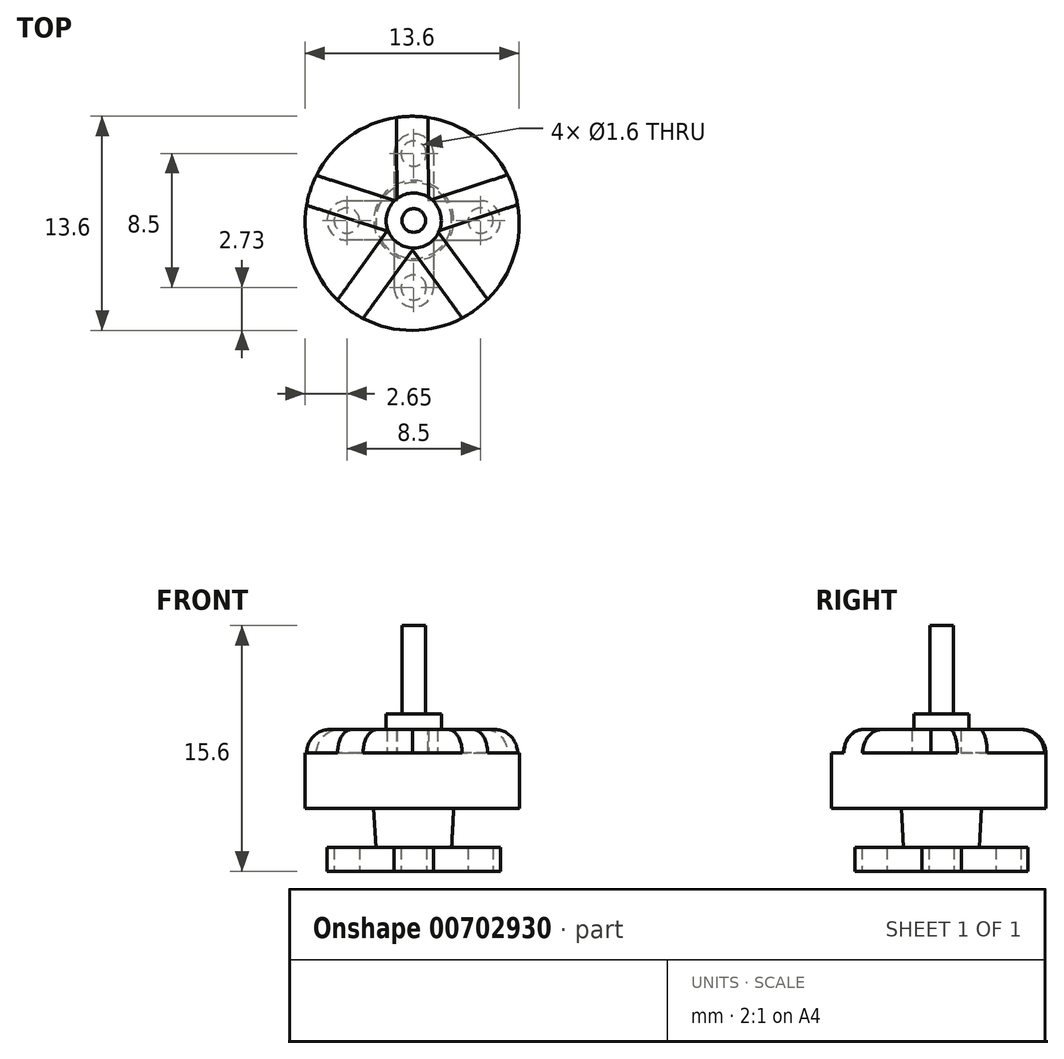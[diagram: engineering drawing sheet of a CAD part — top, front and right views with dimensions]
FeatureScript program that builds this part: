
annotation { "Feature Type Name" : "Feature", "Feature Type Description" : "" }
export const myFeature = defineFeature(function(context is Context, id is Id, definition is map)
    precondition{}
    {
        {
            var Q0;
            Q0=qCreatedBy(makeId("Top.planeOp"),FACE);
            var sketch = newSketch(context, id + "F0", { "sketchPlane" : qUnion([Q0])});
            skLineSegment(sketch, "E0.bottom", {"start": v(0, 0) * mm, "end": v(0, 0) * mm});
            skCircle(sketch, "E1", {"center": v(0, 4.25) * mm, "radius": 0.8 * mm});
            skLineSegment(sketch, "E2", {"start": v(0, 4.25) * mm, "end": v(0, 4.25) * mm});
            skCircle(sketch, "E3", {"center": v(0, -4.25) * mm, "radius": 0.8 * mm});
            skLineSegment(sketch, "E4", {"start": v(0, -4.25) * mm, "end": v(0, -4.25) * mm});
            skLineSegment(sketch, "E5.bottom", {"start": v(0, 1.25) * mm, "end": v(0, -1.25) * mm});
            skLineSegment(sketch, "E5.left", {"start": v(0, 1.25) * mm, "end": v(4.25, 1.25) * mm});
            skLineSegment(sketch, "E5.right", {"start": v(0, -1.25) * mm, "end": v(4.25, -1.25) * mm});
            skCircle(sketch, "E6", {"center": v(4.25, 0) * mm, "radius": 0.8 * mm});
            skArc(sketch, "E7", {"start": v(4.25, 1.25) * mm, "mid": v(5.5, 0) * mm, "end": v(4.25, -1.25) * mm});
            skPoint(sketch, "E8", {"position": v(0, 0) * mm});
            skLineSegment(sketch, "E9.left", {"start": v(0, -1.25) * mm, "end": v(-4.25, -1.25) * mm});
            skLineSegment(sketch, "E9.right", {"start": v(0, 1.25) * mm, "end": v(-4.25, 1.25) * mm});
            skCircle(sketch, "E10", {"center": v(-4.25, 0) * mm, "radius": 0.8 * mm});
            skArc(sketch, "E11", {"start": v(-4.25, -1.25) * mm, "mid": v(-5.5, 0) * mm, "end": v(-4.25, 1.25) * mm});
            skLineSegment(sketch, "E12", {"start": v(-1.25, 4.25) * mm, "end": v(-1.25, 1.25) * mm});
            skLineSegment(sketch, "E13", {"start": v(1.25, 4.25) * mm, "end": v(1.25, 1.25) * mm});
            skArc(sketch, "E14", {"start": v(-1.25, 4.25) * mm, "mid": v(0, 5.5) * mm, "end": v(1.25, 4.25) * mm});
            skLineSegment(sketch, "E15", {"start": v(-1.25, -1.25) * mm, "end": v(-1.25, -4.25) * mm});
            skLineSegment(sketch, "E16", {"start": v(1.25, -1.25) * mm, "end": v(1.25, -4.25) * mm});
            skArc(sketch, "E17", {"start": v(1.25, -4.25) * mm, "mid": v(0, -5.5) * mm, "end": v(-1.25, -4.25) * mm});
            skSolve(sketch);
        }
        {
            var Q0;
            {var subQ1=sQuery(id+"F0.wireOp",EDGE,"E5.bottom");Q0=makeQuery(id+"F0.imprint","IMPRINT",FACE,{"disambiguationData":[TD([[makeQuery(id+"F0.imprint","IMPRINT",EDGE,{"derivedFrom":subQ1}),-1.0]])]});}
            var Q1;
            Q1=makeQuery(id+"F0.imprint","IMPRINT",FACE,{"disambiguationData":[TD([[makeQuery(id+"F0.imprint","IMPRINT",EDGE,{"derivedFrom":sQuery(id+"F0.wireOp",EDGE,"E3")}),-1.0]])]});
            var Q2;
            {var subQ1=sQuery(id+"F0.wireOp",EDGE,"E5.bottom");Q2=makeQuery(id+"F0.imprint","IMPRINT",FACE,{"disambiguationData":[TD([[makeQuery(id+"F0.imprint","IMPRINT",EDGE,{"derivedFrom":subQ1}),1.0]])]});}
            var Q3;
            Q3=makeQuery(id+"F0.imprint","IMPRINT",FACE,{"disambiguationData":[TD([[makeQuery(id+"F0.imprint","IMPRINT",EDGE,{"derivedFrom":sQuery(id+"F0.wireOp",EDGE,"E1")}),-1.0]])]});
            extrude(context, id + "F1", {"entities" : qUnion([Q0, Q1, Q2, Q3]), "depth" : 1.5 * mm, "offsetDistance" : 25 * mm});
        }
        {
            var Q0;
            Q0=qCreatedBy(makeId("Top.planeOp"),FACE);
            var sketch = newSketch(context, id + "F2", { "sketchPlane" : qUnion([Q0])});
            skCircle(sketch, "E18", {"center": v(0, 0) * mm, "radius": 2.33 * mm});
            skSolve(sketch);
        }
        {
            var Q0;
            Q0=qSketchRegion(id+"F2",true);
            extrude(context, id + "F3", {"entities" : qUnion([Q0]), "operationType" : NewBodyOperationType.ADD, "depth" : 4 * mm, "offsetDistance" : 25 * mm, "hasDraft" : true, "draftAngle" : 3 * degree, "hasSecondDirection" : true, "secondDirectionOppositeDirection" : true, "secondDirectionDepth" : -1.5 * mm});
        }
        {
            var Q0;
            Q0=qCreatedBy(makeId("Top.planeOp"),FACE);
            var sketch = newSketch(context, id + "F4", { "sketchPlane" : qUnion([Q0])});
            skCircle(sketch, "E19", {"center": v(-0.1, -0.18) * mm, "radius": 6.8 * mm});
            skLineSegment(sketch, "E20", {"start": v(-4.84, -5.05) * mm, "end": v(-1.07, 0.18) * mm});
            skLineSegment(sketch, "E21", {"start": v(-3.22, -6.22) * mm, "end": v(0.56, -0.98) * mm});
            skLineSegment(sketch, "E22", {"start": v(0.56, -0.98) * mm, "end": v(6.6, 1) * mm});
            skLineSegment(sketch, "E23", {"start": v(5.96, 2.9) * mm, "end": v(-0.09, 0.91) * mm});
            skLineSegment(sketch, "E24", {"start": v(-0.09, 0.91) * mm, "end": v(-6.18, 2.87) * mm});
            skLineSegment(sketch, "E25", {"start": v(-6.8, 0.96) * mm, "end": v(-0.74, -0.98) * mm});
            skLineSegment(sketch, "E26", {"start": v(-0.74, -0.98) * mm, "end": v(3.08, -6.2) * mm});
            skLineSegment(sketch, "E27", {"start": v(4.7, -5) * mm, "end": v(0.93, 0.12) * mm});
            skLineSegment(sketch, "E28", {"start": v(0.93, 0.12) * mm, "end": v(0.9, 6.54) * mm});
            skLineSegment(sketch, "E29", {"start": v(-1.1, 6.55) * mm, "end": v(-1.07, 0.18) * mm});
            skPoint(sketch, "E30", {"position": v(-1.07, 1.23) * mm});
            skPoint(sketch, "E31", {"position": v(0.93, 1.25) * mm});
            skPoint(sketch, "E32", {"position": v(1.51, -0.67) * mm});
            skPoint(sketch, "E33", {"position": v(-0.08, -1.87) * mm});
            skPoint(sketch, "E34", {"position": v(-1.69, -0.68) * mm});
            skSolve(sketch);
        }
        {
            var Q0;
            Q0=makeQuery(id+"F4.imprint","IMPRINT",FACE,{"disambiguationData":[TD([[makeQuery(id+"F4.imprint","IMPRINT",EDGE,{"derivedFrom":sQuery(id+"F4.wireOp",EDGE,"CS8Gledc-ocEL-GRrZ-OUe9-gGzYdw9osQ4W")}),1.0]])]});
            var Q1;
            {var subQ0=sQuery(id+"F4.wireOp",EDGE,"E24");var subQ1=sQuery(id+"F4.wireOp",EDGE,"E19");var subQ2=makeQuery(id+"F4.imprint","INTERSECT",VERTEX,{"derivedFrom":[subQ1,subQ0]});Q1=makeQuery(id+"F4.imprint","IMPRINT",FACE,{"disambiguationData":[TD([[makeQuery(id+"F4.imprint","IMPRINT",EDGE,{"disambiguationData":[TD([[subQ2,1.0]])],"derivedFrom":subQ1}),1.0]])]});}
            var Q2;
            {var subQ0=sQuery(id+"F4.wireOp",EDGE,"E23");var subQ1=sQuery(id+"F4.wireOp",EDGE,"E19");var subQ2=makeQuery(id+"F4.imprint","INTERSECT",VERTEX,{"derivedFrom":[subQ1,subQ0]});Q2=makeQuery(id+"F4.imprint","IMPRINT",FACE,{"disambiguationData":[TD([[makeQuery(id+"F4.imprint","IMPRINT",EDGE,{"disambiguationData":[TD([[subQ2,-1.0]])],"derivedFrom":subQ1}),1.0]])]});}
            var Q3;
            {var subQ0=sQuery(id+"F4.wireOp",EDGE,"E22");var subQ1=sQuery(id+"F4.wireOp",EDGE,"E19");var subQ2=makeQuery(id+"F4.imprint","INTERSECT",VERTEX,{"derivedFrom":[subQ1,subQ0]});Q3=makeQuery(id+"F4.imprint","IMPRINT",FACE,{"disambiguationData":[TD([[makeQuery(id+"F4.imprint","IMPRINT",EDGE,{"disambiguationData":[TD([[subQ2,1.0]])],"derivedFrom":subQ1}),1.0]])]});}
            var Q4;
            {var subQ0=sQuery(id+"F4.wireOp",EDGE,"E21");var subQ1=sQuery(id+"F4.wireOp",EDGE,"E19");var subQ2=makeQuery(id+"F4.imprint","INTERSECT",VERTEX,{"derivedFrom":[subQ1,subQ0]});Q4=makeQuery(id+"F4.imprint","IMPRINT",FACE,{"disambiguationData":[TD([[makeQuery(id+"F4.imprint","IMPRINT",EDGE,{"disambiguationData":[TD([[subQ2,-1.0]])],"derivedFrom":subQ1}),1.0]])]});}
            var Q5;
            {var subQ0=sQuery(id+"F4.wireOp",EDGE,"E20");var subQ1=sQuery(id+"F4.wireOp",EDGE,"E19");var subQ2=makeQuery(id+"F4.imprint","INTERSECT",VERTEX,{"derivedFrom":[subQ1,subQ0]});Q5=makeQuery(id+"F4.imprint","IMPRINT",FACE,{"disambiguationData":[TD([[makeQuery(id+"F4.imprint","IMPRINT",EDGE,{"disambiguationData":[TD([[subQ2,1.0]])],"derivedFrom":subQ1}),1.0]])]});}
            extrude(context, id + "F5", {"entities" : qUnion([Q0, Q1, Q2, Q3, Q4, Q5]), "operationType" : NewBodyOperationType.ADD, "depth" : 7.5 * mm, "offsetDistance" : 25 * mm, "hasSecondDirection" : true, "secondDirectionOppositeDirection" : false, "secondDirectionDepth" : 4 * mm});
        }
        {
            var Q0;
            {var subQ5=sQuery(id+"F4.wireOp",EDGE,"k3woJ1cC-TIMz-5FnJ-hXcG-qWgU7OcKqM6W");var subQ6=sQuery(id+"F4.wireOp",EDGE,"CS8Gledc-ocEL-GRrZ-OUe9-gGzYdw9osQ4W");var subQ7=makeQuery(id+"F4.imprint","INTERSECT",VERTEX,{"derivedFrom":[subQ6,subQ5]});Q0=makeQuery(id+"F4.imprint","IMPRINT",FACE,{"disambiguationData":[TD([[makeQuery(id+"F4.imprint","IMPRINT",EDGE,{"disambiguationData":[TD([[subQ7,-1.0]])],"derivedFrom":subQ6}),1.0]])]});}
            var Q1;
            {var subQ1=sQuery(id+"F4.wireOp",EDGE,"CS8Gledc-ocEL-GRrZ-OUe9-gGzYdw9osQ4W");var subQ5=sQuery(id+"F4.wireOp",EDGE,"syxK5ZXx-2APs-c3Oq-3aUw-kv2rdBUAnRqm");var subQ6=makeQuery(id+"F4.imprint","INTERSECT",VERTEX,{"derivedFrom":[subQ1,subQ5]});Q1=makeQuery(id+"F4.imprint","IMPRINT",FACE,{"disambiguationData":[TD([[makeQuery(id+"F4.imprint","IMPRINT",EDGE,{"disambiguationData":[TD([[subQ6,-1.0]])],"derivedFrom":subQ1}),1.0]])]});}
            var Q2;
            {var subQ1=sQuery(id+"F4.wireOp",EDGE,"CS8Gledc-ocEL-GRrZ-OUe9-gGzYdw9osQ4W");var subQ7=sQuery(id+"F4.wireOp",EDGE,"dCaOjtC0-uw3J-C8sN-ZGMB-qHC1DhSjRnhC");var subQ8=makeQuery(id+"F4.imprint","INTERSECT",VERTEX,{"derivedFrom":[subQ1,subQ7]});Q2=makeQuery(id+"F4.imprint","IMPRINT",FACE,{"disambiguationData":[TD([[makeQuery(id+"F4.imprint","IMPRINT",EDGE,{"disambiguationData":[TD([[subQ8,-1.0]])],"derivedFrom":subQ1}),1.0]])]});}
            var Q3;
            {var subQ13=sQuery(id+"F4.wireOp",EDGE,"raEMwXOy-ZiTj-Mc98-j2ZQ-mD7UlOAf2jAu");var subQ14=sQuery(id+"F4.wireOp",EDGE,"syxK5ZXx-2APs-c3Oq-3aUw-kv2rdBUAnRqm");var subQ15=makeQuery(id+"F4.imprint","INTERSECT",VERTEX,{"derivedFrom":[subQ14,subQ13]});Q3=makeQuery(id+"F4.imprint","IMPRINT",FACE,{"disambiguationData":[TD([[makeQuery(id+"F4.imprint","IMPRINT",EDGE,{"disambiguationData":[TD([[subQ15,1.0]])],"derivedFrom":subQ14}),-1.0]])]});}
            var Q4;
            {var subQ0=sQuery(id+"F4.wireOp",EDGE,"U70CnbfW-tcqK-zMxQ-wlnv-C4eU3dflsgoq");var subQ1=sQuery(id+"F4.wireOp",EDGE,"CS8Gledc-ocEL-GRrZ-OUe9-gGzYdw9osQ4W");var subQ2=makeQuery(id+"F4.imprint","INTERSECT",VERTEX,{"derivedFrom":[subQ1,subQ0]});Q4=makeQuery(id+"F4.imprint","IMPRINT",FACE,{"disambiguationData":[TD([[makeQuery(id+"F4.imprint","IMPRINT",EDGE,{"disambiguationData":[TD([[subQ2,1.0]])],"derivedFrom":subQ1}),1.0]])]});}
            var Q5;
            {var subQ5=sQuery(id+"F4.wireOp",EDGE,"lQARcTSB-Ecui-HiRb-6IBr-9f16AjDH4K86");var subQ6=sQuery(id+"F4.wireOp",EDGE,"CS8Gledc-ocEL-GRrZ-OUe9-gGzYdw9osQ4W");var subQ7=makeQuery(id+"F4.imprint","INTERSECT",VERTEX,{"derivedFrom":[subQ6,subQ5]});Q5=makeQuery(id+"F4.imprint","IMPRINT",FACE,{"disambiguationData":[TD([[makeQuery(id+"F4.imprint","IMPRINT",EDGE,{"disambiguationData":[TD([[subQ7,-1.0]])],"derivedFrom":subQ6}),1.0]])]});}
            var Q6;
            {var subQ5=sQuery(id+"F4.wireOp",EDGE,"E26");var subQ6=sQuery(id+"F4.wireOp",EDGE,"E19");var subQ7=makeQuery(id+"F4.imprint","INTERSECT",VERTEX,{"derivedFrom":[subQ6,subQ5]});Q6=makeQuery(id+"F4.imprint","IMPRINT",FACE,{"disambiguationData":[TD([[makeQuery(id+"F4.imprint","IMPRINT",EDGE,{"disambiguationData":[TD([[subQ7,-1.0]])],"derivedFrom":subQ6}),1.0]])]});}
            var Q7;
            {var subQ1=sQuery(id+"F4.wireOp",EDGE,"E19");var subQ7=sQuery(id+"F4.wireOp",EDGE,"E22");var subQ9=makeQuery(id+"F4.imprint","INTERSECT",VERTEX,{"derivedFrom":[subQ1,subQ7]});Q7=makeQuery(id+"F4.imprint","IMPRINT",FACE,{"disambiguationData":[TD([[makeQuery(id+"F4.imprint","IMPRINT",EDGE,{"disambiguationData":[TD([[subQ9,-1.0]])],"derivedFrom":subQ1}),1.0]])]});}
            var Q8;
            {var subQ5=sQuery(id+"F4.wireOp",EDGE,"E28");var subQ6=sQuery(id+"F4.wireOp",EDGE,"E19");var subQ7=makeQuery(id+"F4.imprint","INTERSECT",VERTEX,{"derivedFrom":[subQ6,subQ5]});Q8=makeQuery(id+"F4.imprint","IMPRINT",FACE,{"disambiguationData":[TD([[makeQuery(id+"F4.imprint","IMPRINT",EDGE,{"disambiguationData":[TD([[subQ7,-1.0]])],"derivedFrom":subQ6}),1.0]])]});}
            var Q9;
            {var subQ1=sQuery(id+"F4.wireOp",EDGE,"E19");var subQ7=sQuery(id+"F4.wireOp",EDGE,"E24");var subQ8=makeQuery(id+"F4.imprint","INTERSECT",VERTEX,{"derivedFrom":[subQ1,subQ7]});Q9=makeQuery(id+"F4.imprint","IMPRINT",FACE,{"disambiguationData":[TD([[makeQuery(id+"F4.imprint","IMPRINT",EDGE,{"disambiguationData":[TD([[subQ8,-1.0]])],"derivedFrom":subQ1}),1.0]])]});}
            var Q10;
            {var subQ1=sQuery(id+"F4.wireOp",EDGE,"E19");var subQ5=sQuery(id+"F4.wireOp",EDGE,"E20");var subQ6=makeQuery(id+"F4.imprint","INTERSECT",VERTEX,{"derivedFrom":[subQ1,subQ5]});Q10=makeQuery(id+"F4.imprint","IMPRINT",FACE,{"disambiguationData":[TD([[makeQuery(id+"F4.imprint","IMPRINT",EDGE,{"disambiguationData":[TD([[subQ6,-1.0]])],"derivedFrom":subQ1}),1.0]])]});}
            var Q11;
            {var subQ13=sQuery(id+"F4.wireOp",EDGE,"E29");var subQ14=sQuery(id+"F4.wireOp",EDGE,"E20");var subQ15=makeQuery(id+"F4.imprint","INTERSECT",VERTEX,{"derivedFrom":[subQ14,subQ13]});Q11=makeQuery(id+"F4.imprint","IMPRINT",FACE,{"disambiguationData":[TD([[makeQuery(id+"F4.imprint","IMPRINT",EDGE,{"disambiguationData":[TD([[subQ15,1.0]])],"derivedFrom":subQ14}),-1.0]])]});}
            extrude(context, id + "F6", {"entities" : qUnion([Q0, Q1, Q2, Q3, Q4, Q5, Q6, Q7, Q8, Q9, Q10, Q11]), "operationType" : NewBodyOperationType.ADD, "depth" : 9 * mm, "offsetDistance" : 25 * mm, "hasSecondDirection" : true, "secondDirectionOppositeDirection" : true, "secondDirectionDepth" : -4 * mm});
        }
        {
            var Q0;
            {var subQ0=sQuery(id+"F4.wireOp",EDGE,"CS8Gledc-ocEL-GRrZ-OUe9-gGzYdw9osQ4W");Q0=makeQuery(id+"F6.opExtrude","CAP_EDGE",EDGE,{"disambiguationData":[OSD([subQ0]),TDD([makeQuery(id+"F4.imprint","IMPRINT",EDGE,{"disambiguationData":[TD([[makeQuery(id+"F4.imprint","INTERSECT",VERTEX,{"derivedFrom":[subQ0,sQuery(id+"F4.wireOp",EDGE,"dCaOjtC0-uw3J-C8sN-ZGMB-qHC1DhSjRnhC")]}),-1.0]])],"derivedFrom":subQ0})])],"isStart":false});}
            var Q1;
            {var subQ0=sQuery(id+"F4.wireOp",EDGE,"CS8Gledc-ocEL-GRrZ-OUe9-gGzYdw9osQ4W");Q1=makeQuery(id+"F6.opExtrude","CAP_EDGE",EDGE,{"disambiguationData":[OSD([subQ0]),TDD([makeQuery(id+"F4.imprint","IMPRINT",EDGE,{"disambiguationData":[TD([[makeQuery(id+"F4.imprint","INTERSECT",VERTEX,{"derivedFrom":[subQ0,sQuery(id+"F4.wireOp",EDGE,"lQARcTSB-Ecui-HiRb-6IBr-9f16AjDH4K86")]}),-1.0]])],"derivedFrom":subQ0})])],"isStart":false});}
            var Q2;
            {var subQ0=sQuery(id+"F4.wireOp",EDGE,"CS8Gledc-ocEL-GRrZ-OUe9-gGzYdw9osQ4W");Q2=makeQuery(id+"F6.opExtrude","CAP_EDGE",EDGE,{"disambiguationData":[OSD([subQ0]),TDD([makeQuery(id+"F4.imprint","IMPRINT",EDGE,{"disambiguationData":[TD([[makeQuery(id+"F4.imprint","INTERSECT",VERTEX,{"derivedFrom":[subQ0,sQuery(id+"F4.wireOp",EDGE,"U70CnbfW-tcqK-zMxQ-wlnv-C4eU3dflsgoq")]}),1.0]])],"derivedFrom":subQ0})])],"isStart":false});}
            var Q3;
            {var subQ0=sQuery(id+"F4.wireOp",EDGE,"CS8Gledc-ocEL-GRrZ-OUe9-gGzYdw9osQ4W");Q3=makeQuery(id+"F6.opExtrude","CAP_EDGE",EDGE,{"disambiguationData":[OSD([subQ0]),TDD([makeQuery(id+"F4.imprint","IMPRINT",EDGE,{"disambiguationData":[TD([[makeQuery(id+"F4.imprint","INTERSECT",VERTEX,{"derivedFrom":[subQ0,sQuery(id+"F4.wireOp",EDGE,"k3woJ1cC-TIMz-5FnJ-hXcG-qWgU7OcKqM6W")]}),-1.0]])],"derivedFrom":subQ0})])],"isStart":false});}
            var Q4;
            {var subQ0=sQuery(id+"F4.wireOp",EDGE,"CS8Gledc-ocEL-GRrZ-OUe9-gGzYdw9osQ4W");Q4=makeQuery(id+"F6.opExtrude","CAP_EDGE",EDGE,{"disambiguationData":[OSD([subQ0]),TDD([makeQuery(id+"F4.imprint","IMPRINT",EDGE,{"disambiguationData":[TD([[makeQuery(id+"F4.imprint","INTERSECT",VERTEX,{"derivedFrom":[subQ0,sQuery(id+"F4.wireOp",EDGE,"syxK5ZXx-2APs-c3Oq-3aUw-kv2rdBUAnRqm")]}),-1.0]])],"derivedFrom":subQ0})])],"isStart":false});}
            var Q5;
            {var subQ0=sQuery(id+"F4.wireOp",EDGE,"E19");Q5=makeQuery(id+"F6.opExtrude","CAP_EDGE",EDGE,{"disambiguationData":[OSD([subQ0]),TDD([makeQuery(id+"F4.imprint","IMPRINT",EDGE,{"disambiguationData":[TD([[makeQuery(id+"F4.imprint","INTERSECT",VERTEX,{"derivedFrom":[subQ0,sQuery(id+"F4.wireOp",EDGE,"E28")]}),-1.0]])],"derivedFrom":subQ0})])],"isStart":false});}
            var Q6;
            {var subQ0=sQuery(id+"F4.wireOp",EDGE,"E19");Q6=makeQuery(id+"F6.opExtrude","CAP_EDGE",EDGE,{"disambiguationData":[OSD([subQ0]),TDD([makeQuery(id+"F4.imprint","IMPRINT",EDGE,{"disambiguationData":[TD([[makeQuery(id+"F4.imprint","INTERSECT",VERTEX,{"derivedFrom":[subQ0,sQuery(id+"F4.wireOp",EDGE,"E24")]}),-1.0]])],"derivedFrom":subQ0})])],"isStart":false});}
            var Q7;
            {var subQ0=sQuery(id+"F4.wireOp",EDGE,"E19");Q7=makeQuery(id+"F6.opExtrude","CAP_EDGE",EDGE,{"disambiguationData":[OSD([subQ0]),TDD([makeQuery(id+"F4.imprint","IMPRINT",EDGE,{"disambiguationData":[TD([[makeQuery(id+"F4.imprint","INTERSECT",VERTEX,{"derivedFrom":[subQ0,sQuery(id+"F4.wireOp",EDGE,"E20")]}),-1.0]])],"derivedFrom":subQ0})])],"isStart":false});}
            var Q8;
            {var subQ0=sQuery(id+"F4.wireOp",EDGE,"E19");Q8=makeQuery(id+"F6.opExtrude","CAP_EDGE",EDGE,{"disambiguationData":[OSD([subQ0]),TDD([makeQuery(id+"F4.imprint","IMPRINT",EDGE,{"disambiguationData":[TD([[makeQuery(id+"F4.imprint","INTERSECT",VERTEX,{"derivedFrom":[subQ0,sQuery(id+"F4.wireOp",EDGE,"E22")]}),-1.0]])],"derivedFrom":subQ0})])],"isStart":false});}
            var Q9;
            {var subQ0=sQuery(id+"F4.wireOp",EDGE,"E19");Q9=makeQuery(id+"F6.opExtrude","CAP_EDGE",EDGE,{"disambiguationData":[OSD([subQ0]),TDD([makeQuery(id+"F4.imprint","IMPRINT",EDGE,{"disambiguationData":[TD([[makeQuery(id+"F4.imprint","INTERSECT",VERTEX,{"derivedFrom":[subQ0,sQuery(id+"F4.wireOp",EDGE,"E26")]}),-1.0]])],"derivedFrom":subQ0})])],"isStart":false});}
            fillet(context, id + "F7", {"entities" : qUnion([Q0, Q1, Q2, Q3, Q4, Q5, Q6, Q7, Q8, Q9]), "radius" : 1.5 * mm, "tangentPropagation" : true, "allowEdgeOverflow" : false});
        }
        {
            var Q0;
            Q0=qCreatedBy(makeId("Top.planeOp"),FACE);
            var sketch = newSketch(context, id + "F8", { "sketchPlane" : qUnion([Q0])});
            skCircle(sketch, "E35", {"center": v(0, 0) * mm, "radius": 1.75 * mm});
            skCircle(sketch, "E36", {"center": v(0, 0) * mm, "radius": 0.75 * mm});
            skSolve(sketch);
        }
        {
            var Q0;
            Q0=makeQuery(id+"F8.imprint","IMPRINT",FACE,{"disambiguationData":[TD([[makeQuery(id+"F8.imprint","IMPRINT",EDGE,{"derivedFrom":sQuery(id+"F8.wireOp",EDGE,"E36")}),1.0]])]});
            var Q1;
            Q1=makeQuery(id+"F8.imprint","IMPRINT",FACE,{"disambiguationData":[TD([[makeQuery(id+"F8.imprint","IMPRINT",EDGE,{"derivedFrom":sQuery(id+"F8.wireOp",EDGE,"E35")}),1.0]])]});
            var Q2;
            Q2=sQuery(id+"F8.wireOp",EDGE,"E35");
            extrude(context, id + "F9", {"entities" : qUnion([Q0, Q1]), "operationType" : NewBodyOperationType.ADD, "surfaceEntities" : qUnion([Q2]), "depth" : 10 * mm, "offsetDistance" : 25 * mm, "hasSecondDirection" : true, "secondDirectionOppositeDirection" : false, "secondDirectionDepth" : 9 * mm});
        }
        {
            var Q0;
            Q0=makeQuery(id+"F8.imprint","IMPRINT",FACE,{"disambiguationData":[TD([[makeQuery(id+"F8.imprint","IMPRINT",EDGE,{"derivedFrom":sQuery(id+"F8.wireOp",EDGE,"E36")}),1.0]])]});
            extrude(context, id + "F10", {"entities" : qUnion([Q0]), "operationType" : NewBodyOperationType.ADD, "depth" : 15.6 * mm, "offsetDistance" : 25 * mm});
        }
    });
